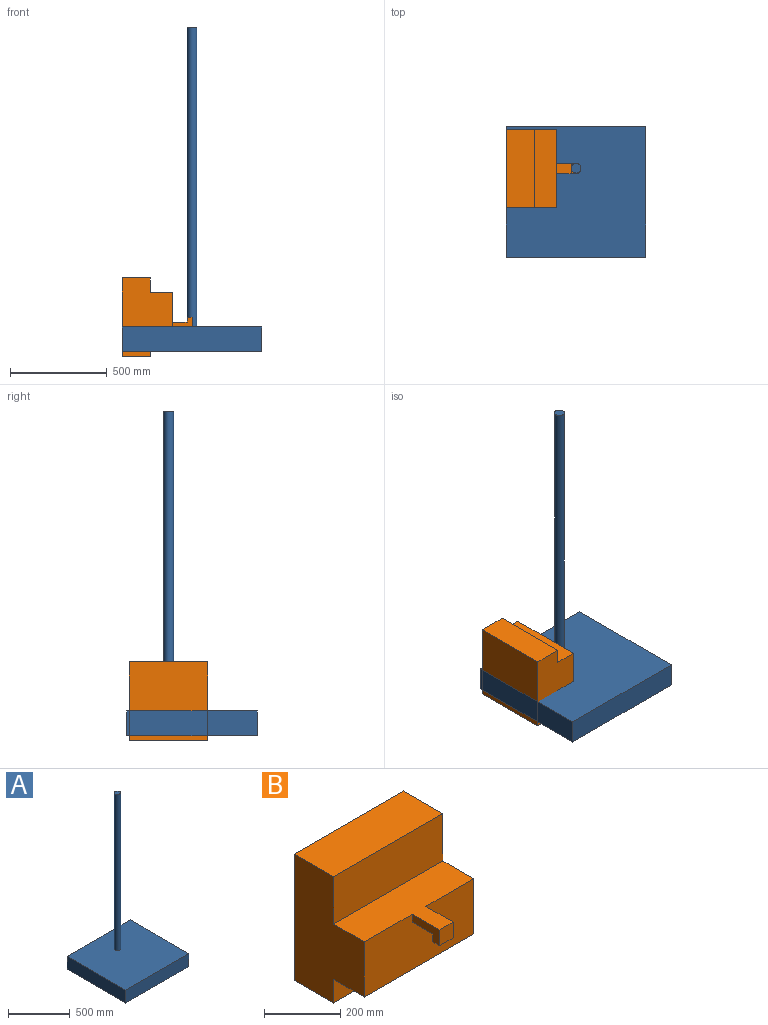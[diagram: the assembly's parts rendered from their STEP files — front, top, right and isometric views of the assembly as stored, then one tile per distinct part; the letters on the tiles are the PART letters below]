
ASSEMBLY  parts=2 mates=1
PART A: 8 faces, bbox 723.9x673.1x1676.4 mm
  f0: plane 673.1x127mm, normal (1,0,0), area 85483.7mm2, adj f1,f3,f4,f5
  f1: plane 723.9x127mm, normal (0,1,0), area 91935.3mm2, adj f0,f2,f4,f5
  f2: plane 673.1x127mm, normal (-1,0,0), area 85483.7mm2, adj f1,f3,f4,f5
  f3: plane 723.9x127mm, normal (0,-1,0), area 91935.3mm2, adj f0,f2,f4,f5
  f4: plane 723.9x673.1mm, normal (0,0,1), area 485230.3mm2, adj f0,f1,f2,f3,f6
  f5: plane 723.9x673.1mm, normal (0,0,-1), area 487257.1mm2, adj f0,f1,f2,f3
  f6: cylinder r=25.4mm len=1549.4mm, axis (0,0,-1), area 247273.2mm2, adj f4,f7
  f7: plane 50.8x50.8mm, normal (0,0,1), area 2026.8mm2, adj f6
PART B: 16 faces, bbox 406.4x362x406.4 mm
  f0: plane 101.6x50.8mm, normal (1,0,0), area 3225.8mm2, adj f1,f3,f4,f5,f6,f7
  f1: plane 50.8x25.4mm, normal (0,1,0), area 1290.3mm2, adj f0,f2,f4,f6
  f2: plane 101.6x50.8mm, normal (-1,0,0), area 3225.8mm2, adj f1,f3,f4,f5,f6,f7
  f3: plane 50.8x50.8mm, normal (0,-1,0), area 2580.6mm2, adj f0,f2,f4,f5
  f4: plane 50.8x25.4mm, normal (0,0,-1), area 1290.3mm2, adj f0,f1,f2,f3
  f5: plane 406.4x215.9mm, normal (0,0,1), area 51612.8mm2, adj f0,f2,f3,f7,f8,f9,f11
  f6: plane 76.2x50.8mm, normal (0,0,-1), area 3871mm2, adj f0,f1,f2,f7
  f7: plane 406.4x177.8mm, normal (0,-1,0), area 70967.6mm2, adj f0,f2,f5,f6,f8,f9,f10
  f8: plane 406.4x260.35mm, normal (1,0,0), area 79677.3mm2, adj f5,f7,f10,f11,f12,f13,f14,f15
  f9: plane 406.4x260.35mm, normal (-1,0,0), area 79677.3mm2, adj f5,f7,f10,f11,f12,f13,f14,f15
  f10: plane 406.4x114.3mm, normal (0,0,-1), area 46451.5mm2, adj f7,f8,f9,f12
  f11: plane 406.4x152.4mm, normal (0,-1,0), area 61935.4mm2, adj f5,f8,f9,f14
  f12: plane 406.4x76.2mm, normal (0,-1,0), area 30967.7mm2, adj f8,f9,f10,f15
  f13: plane 406.4x406.4mm, normal (0,1,0), area 165161mm2, adj f8,f9,f14,f15
  f14: plane 406.4x146.05mm, normal (0,0,1), area 59354.7mm2, adj f8,f9,f11,f13
  f15: plane 406.4x146.05mm, normal (0,0,-1), area 59354.7mm2, adj f8,f9,f12,f13
PLACE A t=(-535.63,117.15,-142.25)mm fixed
PLACE B rot(axis=(0.71,-0.71,0),180deg) t=(-705.3,212.4,-15.25)mm
MATE cylindrical B.f5 <-> A.f6  axis (0,0,-1) through (-535.63,237.8,-15.25)mm
